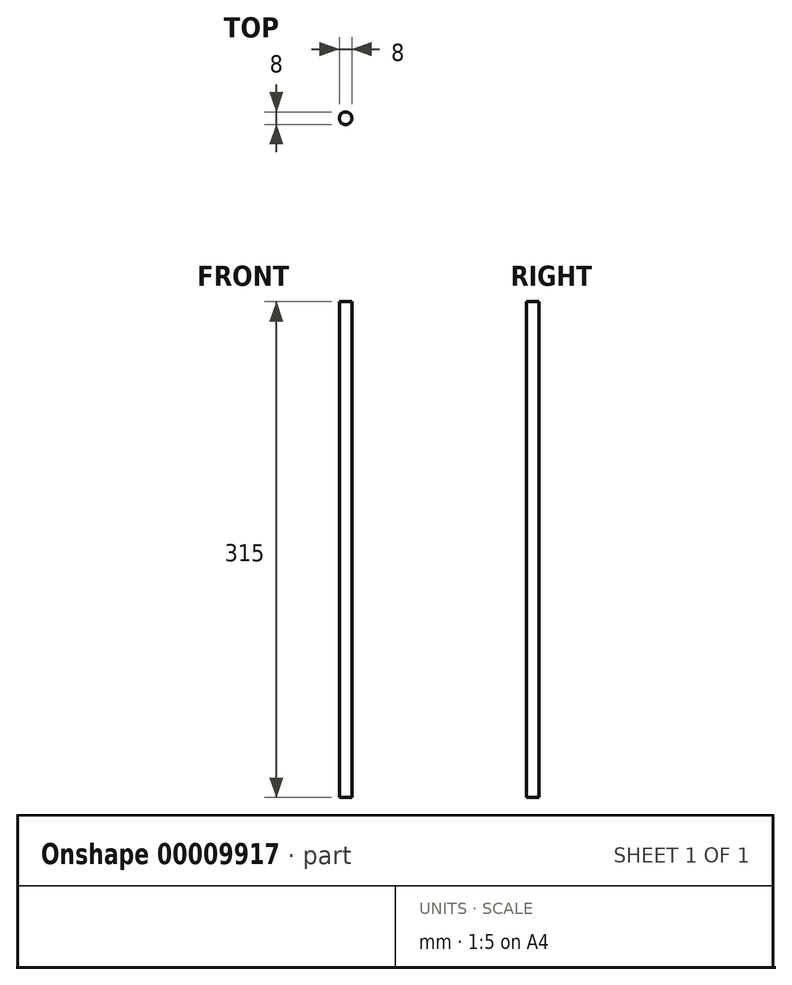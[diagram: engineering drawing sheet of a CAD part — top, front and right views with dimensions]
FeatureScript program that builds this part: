
annotation { "Feature Type Name" : "Feature", "Feature Type Description" : "" }
export const myFeature = defineFeature(function(context is Context, id is Id, definition is map)
    precondition{}
    {
        {
            var Q0;
            Q0=qCreatedBy(makeId("Top.planeOp"),FACE);
            var sketch = newSketch(context, id + "F0", { "sketchPlane" : qUnion([Q0])});
            skCircle(sketch, "E0", {"center": v(0, 0) * mm, "radius": 4 * mm});
            skSolve(sketch);
        }
        {
            var Q0;
            Q0 = qSketchRegion(id + "F0", true);
            extrude(context, id + "F1", {"entities" : qUnion([Q0]), "depth" : 315 * mm});
        }
    });
